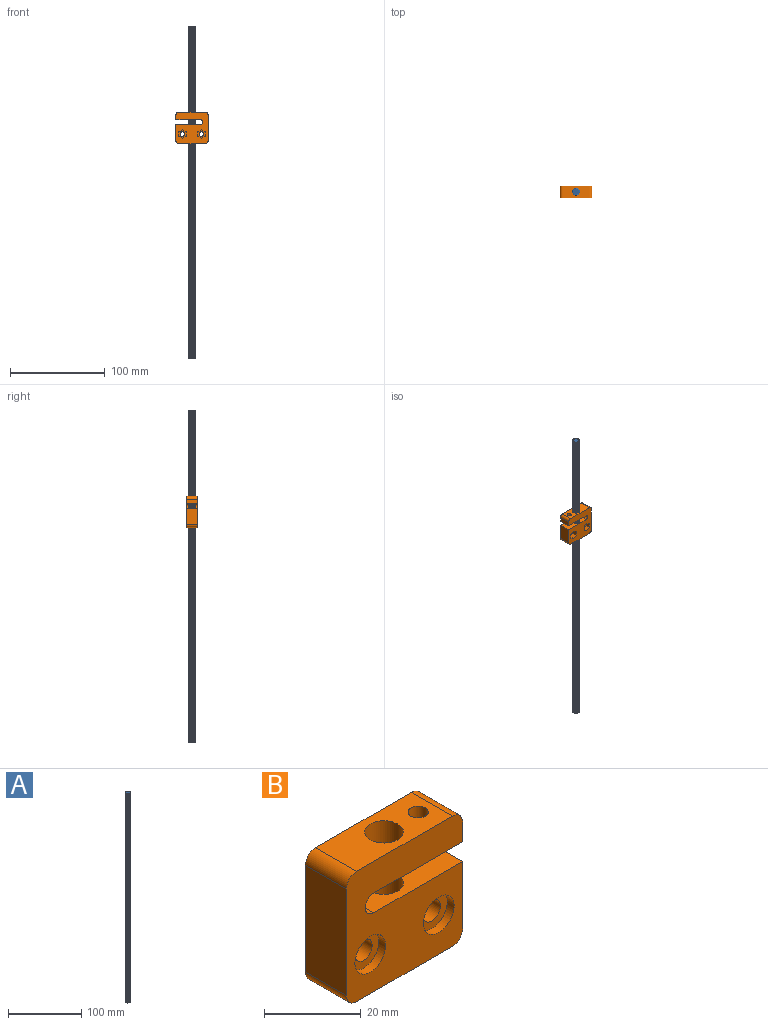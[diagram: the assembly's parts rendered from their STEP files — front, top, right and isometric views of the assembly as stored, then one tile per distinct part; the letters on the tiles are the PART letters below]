
ASSEMBLY  parts=2 mates=1
PART A: 27 faces, bbox 8x8x351 mm
  f0: cylinder r=4mm len=349mm, axis (0,0,-1), area 1253.1mm2, adj f3,f6,f12,f14,f21
  f1: cylinder r=4mm len=349mm, axis (0,0,-1), area 1253.1mm2, adj f5,f6,f16,f18,f25
  f2: plane 7x7mm, normal (0,0,-1), area 33.4mm2, adj f3,f4,f5,f9,f11,f12,f13,f15
  f3: cone r=4mm half-angle=45deg, axis (0,0,1), area 2.1mm2, adj f0,f2,f12,f21
  f4: cone r=4mm half-angle=45deg, axis (0,0,1), area 2.1mm2, adj f2,f8,f13,f24
  f5: cone r=4mm half-angle=45deg, axis (0,0,1), area 2.1mm2, adj f1,f2,f16,f25
  f6: cone r=3.5mm half-angle=45deg, axis (0,0,-1), area 14.6mm2, adj f0,f1,f7,f8,f10,f13,f14,f17
  f7: cylinder r=4mm len=349mm, axis (0,0,-1), area 1253.1mm2, adj f6,f9,f17,f20,f22
  f8: cylinder r=4mm len=349mm, axis (0,0,-1), area 1253.1mm2, adj f4,f6,f13,f24,f26
  f9: cone r=4mm half-angle=45deg, axis (0,0,1), area 2.1mm2, adj f2,f7,f17,f20
  f10: plane 7x7mm, normal (0,0,1), area 38.5mm2, adj f6
  f11: cylinder r=3mm len=349.99mm, axis (0,0,1), area 1978.7mm2, adj f2,f12,f13,f14
  f12: bspline ~350x8mm, area 1020.3mm2, adj f0,f2,f3,f11,f14
  f13: bspline ~351x8mm, area 1027.4mm2, adj f2,f4,f6,f8,f11,f14
  f14: plane 1x1mm, normal (0,-1,0), area 0.9mm2, adj f0,f6,f11,f12,f13
  f15: cylinder r=3mm len=349.99mm, axis (0,0,1), area 1978.7mm2, adj f2,f16,f17,f18
  f16: bspline ~349x8mm, area 1021.8mm2, adj f1,f2,f5,f15,f18
  f17: bspline ~351x8mm, area 1021.9mm2, adj f2,f6,f7,f9,f15,f18
  f18: plane 1x1mm, normal (0,1,0), area 0.9mm2, adj f1,f6,f15,f16,f17
  f19: cylinder r=3mm len=349.99mm, axis (0,0,1), area 1978.7mm2, adj f2,f20,f21,f22
  f20: bspline ~350x8mm, area 1020.3mm2, adj f2,f7,f9,f19,f22
  f21: bspline ~351x8mm, area 1027.4mm2, adj f0,f2,f3,f6,f19,f22
  f22: plane 1x1mm, normal (-1,0,0), area 0.9mm2, adj f6,f7,f19,f20,f21
  f23: cylinder r=3mm len=349.99mm, axis (0,0,1), area 1978.7mm2, adj f2,f24,f25,f26
  f24: bspline ~349x8mm, area 1021.8mm2, adj f2,f4,f8,f23,f26
  f25: bspline ~351x8mm, area 1021.9mm2, adj f1,f2,f5,f6,f23,f26
  f26: plane 1x1mm, normal (1,0,0), area 0.9mm2, adj f6,f8,f23,f24,f25
PART B: 37 faces, bbox 34x12x33 mm
  f0: cylinder r=2.1mm len=8mm, axis (0,0,1), area 105.6mm2, adj f13,f31
  f1: cylinder r=2.5mm len=12mm, axis (0,1,0), area 94.2mm2, adj f10,f12,f31,f32
  f2: cylinder r=4.5mm len=9mm, axis (0,-1,0), area 56.5mm2, adj f10,f30
  f3: cylinder r=4.5mm len=9mm, axis (0,-1,0), area 56.5mm2, adj f10,f29
  f4: cylinder r=4mm len=20mm, axis (0,0,1), area 502.7mm2, adj f14,f32
  f5: cylinder r=2.55mm len=5.1mm, axis (0,1,0), area 80.1mm2, adj f22,f29
  f6: cylinder r=2.55mm len=5.1mm, axis (0,1,0), area 80.1mm2, adj f15,f30
  f7: cylinder r=4mm len=8mm, axis (0,0,1), area 201.1mm2, adj f13,f31
  f8: plane 12x5mm, normal (1,0,0), area 60mm2, adj f10,f12,f31,f35
  f9: plane 27x12mm, normal (-1,0,0), area 324mm2, adj f10,f12,f33,f36
  f10: plane 34x33mm, normal (0,-1,0), area 847.2mm2, adj f1,f2,f3,f8,f9,f11,f13,f14
  f11: plane 17x12mm, normal (1,0,0), area 204mm2, adj f10,f12,f32,f34
  f12: plane 34x33mm, normal (0,1,0), area 863.6mm2, adj f1,f8,f9,f11,f13,f14,f16,f17
  f13: plane 28x12mm, normal (0,0,1), area 271.9mm2, adj f0,f7,f10,f12,f35,f36
  f14: plane 28x12mm, normal (0,0,-1), area 285.7mm2, adj f4,f10,f12,f33,f34
  f15: plane 9.24x8mm, normal (0,1,0), area 35mm2, adj f6,f16,f17,f18,f19,f20,f21
  f16: plane 5x4mm, normal (-0.5,0,0.87), area 23.1mm2, adj f12,f15,f17,f21
  f17: plane 5x4.62mm, normal (-1,0,0), area 23.1mm2, adj f12,f15,f16,f18
  f18: plane 5x4mm, normal (-0.5,0,-0.87), area 23.1mm2, adj f12,f15,f17,f19
  f19: plane 5x4mm, normal (0.5,0,-0.87), area 23.1mm2, adj f12,f15,f18,f20
  f20: plane 5x4.62mm, normal (1,0,0), area 23.1mm2, adj f12,f15,f19,f21
  f21: plane 5x4mm, normal (0.5,0,0.87), area 23.1mm2, adj f12,f15,f16,f20
  f22: plane 9.24x8mm, normal (0,1,0), area 35mm2, adj f5,f23,f24,f25,f26,f27,f28
  f23: plane 5x4.62mm, normal (1,0,0), area 23.1mm2, adj f12,f22,f24,f28
  f24: plane 5x4mm, normal (0.5,0,0.87), area 23.1mm2, adj f12,f22,f23,f25
  f25: plane 5x4mm, normal (-0.5,0,0.87), area 23.1mm2, adj f12,f22,f24,f26
  f26: plane 5x4.62mm, normal (-1,0,0), area 23.1mm2, adj f12,f22,f25,f27
  f27: plane 5x4mm, normal (-0.5,0,-0.87), area 23.1mm2, adj f12,f22,f26,f28
  f28: plane 5x4mm, normal (0.5,0,-0.87), area 23.1mm2, adj f12,f22,f23,f27
  f29: plane 9x9mm, normal (0,-1,0), area 43.2mm2, adj f3,f5
  f30: plane 9x9mm, normal (0,-1,0), area 43.2mm2, adj f2,f6
  f31: plane 26x12mm, normal (0,0,-1), area 247.9mm2, adj f0,f1,f7,f8,f10,f12
  f32: plane 26x12mm, normal (0,0,1), area 261.7mm2, adj f1,f4,f10,f11,f12
  f33: cylinder r=3mm len=12mm, axis (0,-1,0), area 56.5mm2, adj f9,f10,f12,f14
  f34: cylinder r=3mm len=12mm, axis (0,1,0), area 56.5mm2, adj f10,f11,f12,f14
  f35: cylinder r=3mm len=12mm, axis (0,-1,0), area 56.5mm2, adj f8,f10,f12,f13
  f36: cylinder r=3mm len=12mm, axis (0,1,0), area 56.5mm2, adj f9,f10,f12,f13
PLACE A rot(axis=(0.64,-0.77,0),180deg) t=(-162.37,189.11,252.84)mm
PLACE B rot(axis=(0,0,-1),179.7deg) t=(-162.37,189.11,128.96)mm
MATE cylindrical B.f4 <-> A.f0  axis (0,0,1) through (-162.37,189.11,161.96)mm
